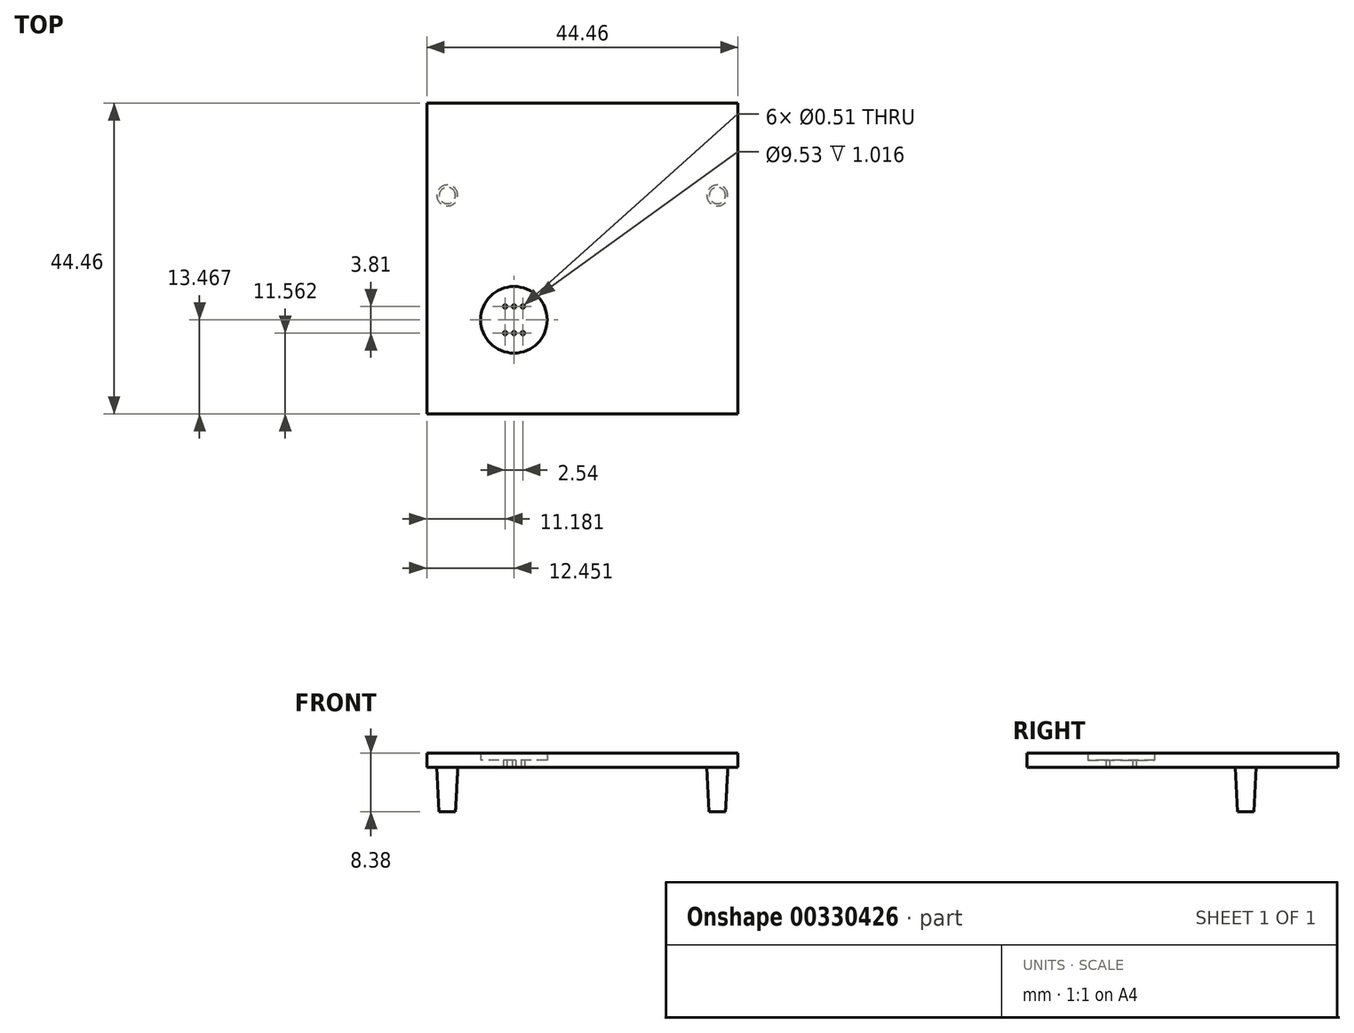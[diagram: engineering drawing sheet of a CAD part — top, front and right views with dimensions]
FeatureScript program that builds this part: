
annotation { "Feature Type Name" : "Feature", "Feature Type Description" : "" }
export const myFeature = defineFeature(function(context is Context, id is Id, definition is map)
    precondition{}
    {
        {
            var Q0;
            Q0=qCreatedBy(makeId("Top.planeOp"),FACE);
            var sketch = newSketch(context, id + "F0", { "sketchPlane" : qUnion([Q0])});
            skLineSegment(sketch, "E0.bottom", {"start": v(22.23, 22.22) * mm, "end": v(-22.23, 22.22) * mm});
            skLineSegment(sketch, "E0.top", {"start": v(22.23, -22.23) * mm, "end": v(-22.23, -22.23) * mm});
            skLineSegment(sketch, "E0.left", {"start": v(22.23, 22.22) * mm, "end": v(22.23, -22.23) * mm});
            skLineSegment(sketch, "E0.right", {"start": v(-22.23, 22.22) * mm, "end": v(-22.23, -22.23) * mm});
            skPoint(sketch, "E0.middle", {"position": v(0, 0) * mm});
            skSolve(sketch);
        }
        {
            var Q0;
            Q0 = qSketchRegion(id + "F0", true);
            extrude(context, id + "F1", {"entities" : qUnion([Q0]), "depth" : 2.03 * mm});
        }
        {
            var Q0;
            Q0=qCreatedBy(makeId("Top.planeOp"),FACE);
            var sketch = newSketch(context, id + "F2", { "sketchPlane" : qUnion([Q0])});
            skCircle(sketch, "E1", {"center": v(-19.3, 9.02) * mm, "radius": 1.5 * mm});
            skCircle(sketch, "E2.MirrorC", {"center": v(19.3, 9.02) * mm, "radius": 1.5 * mm});
            skSolve(sketch);
        }
        {
            var Q0;
            Q0 = qSketchRegion(id + "F2", true);
            extrude(context, id + "F3", {"entities" : qUnion([Q0]), "operationType" : NewBodyOperationType.ADD, "oppositeDirection" : true, "depth" : 6.35 * mm, "hasDraft" : true, "draftAngle" : 3 * degree, "draftPullDirection" : true});
        }
        {
            var Q0;
            Q0=qCreatedBy(makeId("Top.planeOp"),FACE);
            var sketch = newSketch(context, id + "F4", { "sketchPlane" : qUnion([Q0])});
            skCircle(sketch, "E3", {"center": v(-11.05, -6.86) * mm, "radius": 0.25 * mm});
            skCircle(sketch, "E4.0.1.0", {"center": v(-11.05, -10.67) * mm, "radius": 0.25 * mm});
            skCircle(sketch, "E4.1.0.0", {"center": v(-9.78, -6.86) * mm, "radius": 0.25 * mm});
            skCircle(sketch, "E4.1.1.0", {"center": v(-9.78, -10.67) * mm, "radius": 0.25 * mm});
            skCircle(sketch, "E4.2.0.0", {"center": v(-8.5, -6.86) * mm, "radius": 0.25 * mm});
            skCircle(sketch, "E4.2.1.0", {"center": v(-8.5, -10.67) * mm, "radius": 0.25 * mm});
            skLineSegment(sketch, "E4.direction1", {"start": v(-11.05, -6.86) * mm, "end": v(-9.78, -6.86) * mm, "construction": true});
            skLineSegment(sketch, "E4.direction2", {"start": v(-11.05, -6.86) * mm, "end": v(-11.05, -10.67) * mm, "construction": true});
            skSolve(sketch);
        }
        {
            var Q0;
            Q0 = qSketchRegion(id + "F4", true);
            extrude(context, id + "F5", {"entities" : qUnion([Q0]), "operationType" : NewBodyOperationType.REMOVE, "depth" : 25.4 * mm});
        }
        {
            var Q0;
            Q0=qCreatedBy(makeId("Top.planeOp"),FACE);
            var sketch = newSketch(context, id + "F6", { "sketchPlane" : qUnion([Q0])});
            skCircle(sketch, "E5", {"center": v(-9.78, -8.76) * mm, "radius": 4.76 * mm});
            skLineSegment(sketch, "E6", {"start": v(-9.78, -6.86) * mm, "end": v(-9.78, -10.67) * mm, "construction": true});
            skSolve(sketch);
        }
        {
            var Q0;
            Q0 = qSketchRegion(id + "F6", true);
            var Q1;
            Q1=makeQuery(id+"F1.opExtrude","CAP_FACE",FACE,{"disambiguationData":[OSD([sQuery(id+"F0.wireOp",EDGE,"E0.bottom"),sQuery(id+"F0.wireOp",EDGE,"E0.top"),sQuery(id+"F0.wireOp",EDGE,"E0.left"),sQuery(id+"F0.wireOp",EDGE,"E0.right")])],"isStart":false});
            extrude(context, id + "F7", {"entities" : qUnion([Q0]), "operationType" : NewBodyOperationType.REMOVE, "endBound" : BoundingType.UP_TO_SURFACE, "endBoundEntityFace" : qUnion([Q1]), "depth" : 25.4 * mm, "hasSecondDirection" : true, "secondDirectionOppositeDirection" : false, "secondDirectionDepth" : 1.02 * mm});
        }
    });
